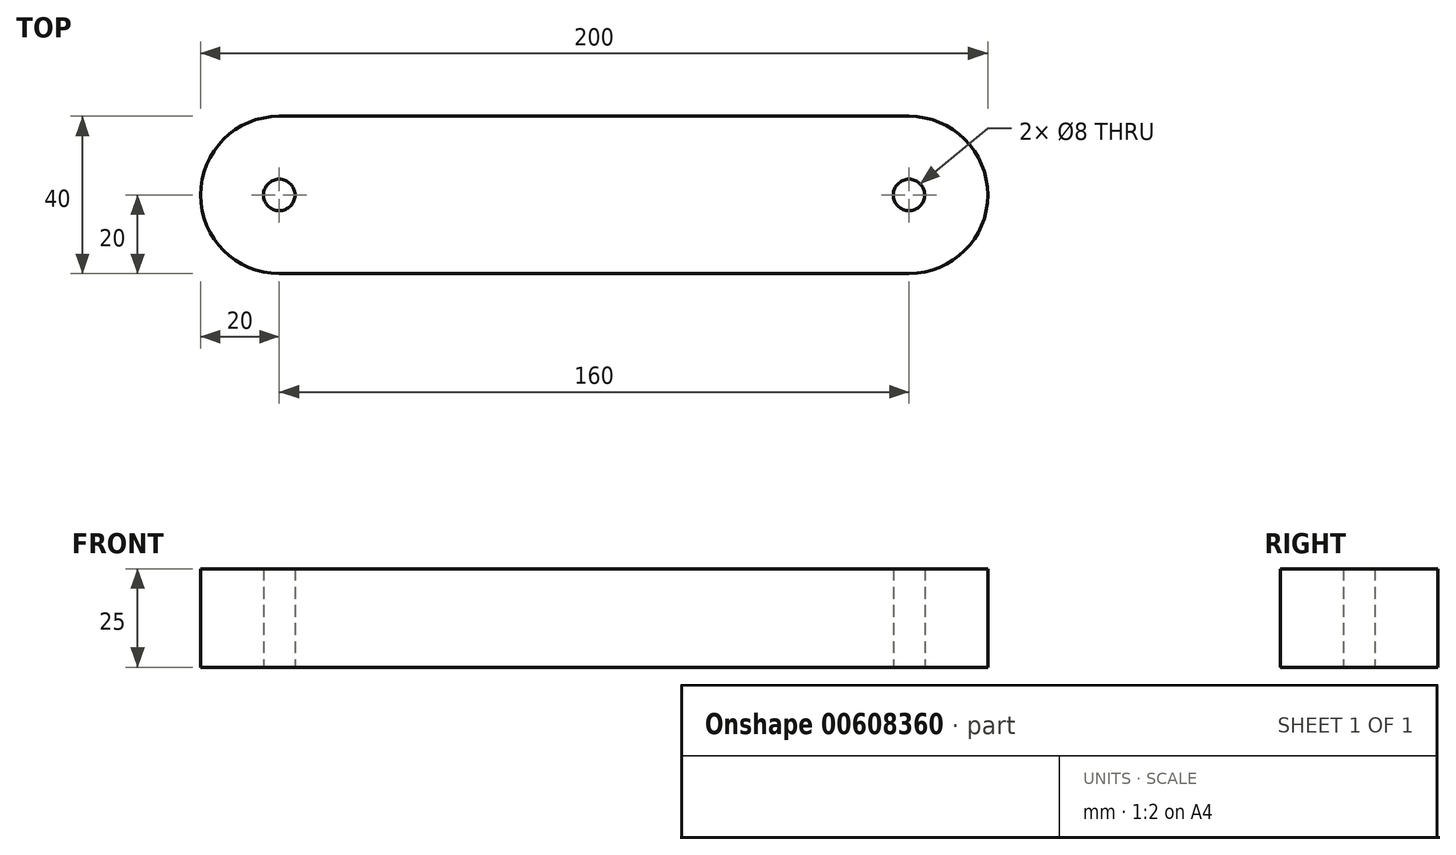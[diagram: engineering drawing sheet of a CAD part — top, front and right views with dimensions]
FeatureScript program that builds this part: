
annotation { "Feature Type Name" : "Feature", "Feature Type Description" : "" }
export const myFeature = defineFeature(function(context is Context, id is Id, definition is map)
    precondition{}
    {
        {
            var Q0;
            Q0=qCreatedBy(makeId("Top.planeOp"),FACE);
            var sketch = newSketch(context, id + "F0", { "sketchPlane" : qUnion([Q0])});
            skLineSegment(sketch, "E0.bottom", {"start": v(80, -20) * mm, "end": v(-80, -20) * mm});
            skLineSegment(sketch, "E0.top", {"start": v(80, 20) * mm, "end": v(-80, 20) * mm});
            skPoint(sketch, "E0.middle", {"position": v(0, 0) * mm});
            skCircle(sketch, "E1", {"center": v(-80, 0) * mm, "radius": 4 * mm});
            skCircle(sketch, "E2.MirrorC", {"center": v(80, 0) * mm, "radius": 4 * mm});
            skArc(sketch, "E3", {"start": v(-80, 20) * mm, "mid": v(-100, 0) * mm, "end": v(-80, -20) * mm});
            skArc(sketch, "E4.MirrorC", {"start": v(80, 20) * mm, "mid": v(100, 0) * mm, "end": v(80, -20) * mm});
            skSolve(sketch);
        }
        {
            var Q0;
            Q0=makeQuery(id+"F0.imprint","IMPRINT",FACE,{"disambiguationData":[TD([[makeQuery(id+"F0.imprint","IMPRINT",EDGE,{"derivedFrom":sQuery(id+"F0.wireOp",EDGE,"E0.bottom")}),-1.0]])]});
            extrude(context, id + "F1", {"entities" : qUnion([Q0]), "depth" : 25 * mm, "offsetDistance" : 25 * mm});
        }
    });
